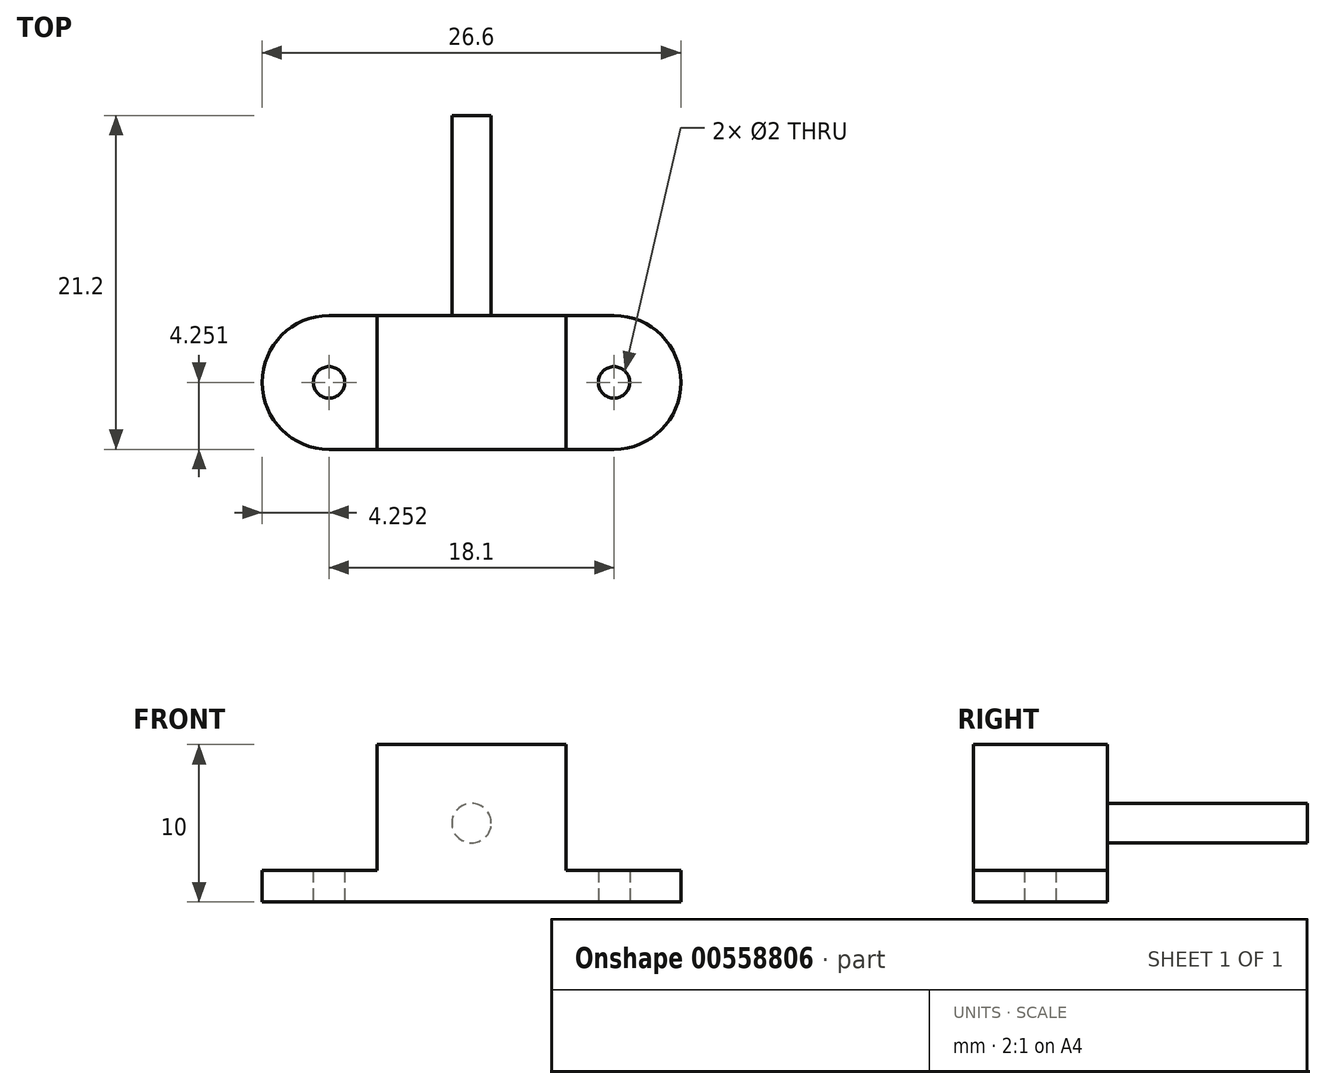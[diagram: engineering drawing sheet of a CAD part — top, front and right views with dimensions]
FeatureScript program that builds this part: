
annotation { "Feature Type Name" : "Feature", "Feature Type Description" : "" }
export const myFeature = defineFeature(function(context is Context, id is Id, definition is map)
    precondition{}
    {
        {
            var Q0;
            Q0=qCreatedBy(makeId("Top.planeOp"),FACE);
            var sketch = newSketch(context, id + "F0", { "sketchPlane" : qUnion([Q0])});
            skLineSegment(sketch, "E0.bottom", {"start": v(-10.3, -6.4) * mm, "end": v(16.3, -6.4) * mm});
            skLineSegment(sketch, "E0.top", {"start": v(-10.3, 2.1) * mm, "end": v(16.3, 2.1) * mm});
            skLineSegment(sketch, "E0.left", {"start": v(-10.3, -6.4) * mm, "end": v(-10.3, 2.1) * mm});
            skLineSegment(sketch, "E0.right", {"start": v(16.3, -6.4) * mm, "end": v(16.3, 2.1) * mm});
            skArc(sketch, "E1", {"start": v(-6.06, 2.1) * mm, "mid": v(-10.3, -2.15) * mm, "end": v(-6.06, -6.4) * mm});
            skArc(sketch, "E2", {"start": v(12.04, -6.4) * mm, "mid": v(16.3, -2.15) * mm, "end": v(12.04, 2.1) * mm});
            skCircle(sketch, "E3", {"center": v(-6.06, -2.15) * mm, "radius": 1 * mm});
            skCircle(sketch, "E4", {"center": v(12.04, -2.15) * mm, "radius": 1 * mm});
            skSolve(sketch);
        }
        {
            var Q0;
            Q0=makeQuery(id+"F0.imprint","IMPRINT",FACE,{"disambiguationData":[TD([[makeQuery(id+"F0.imprint","IMPRINT",EDGE,{"derivedFrom":sQuery(id+"F0.wireOp",EDGE,"E3")}),-1.0]])]});
            extrude(context, id + "F1", {"entities" : qUnion([Q0]), "depth" : 2 * mm, "offsetDistance" : 25.4 * mm});
        }
        {
            var Q0;
            Q0=makeQuery(id+"F1.opExtrude","CAP_FACE",FACE,{"disambiguationData":[OSD([sQuery(id+"F0.wireOp",EDGE,"E0.bottom"),sQuery(id+"F0.wireOp",EDGE,"E0.top"),sQuery(id+"F0.wireOp",EDGE,"E1"),sQuery(id+"F0.wireOp",EDGE,"E2"),sQuery(id+"F0.wireOp",EDGE,"E3"),sQuery(id+"F0.wireOp",EDGE,"E4")])],"isStart":false});
            var sketch = newSketch(context, id + "F2", { "sketchPlane" : qUnion([Q0])});
            skLineSegment(sketch, "E5.bottom", {"start": v(-10.3, -6.4) * mm, "end": v(16.3, -6.4) * mm});
            skLineSegment(sketch, "E5.top", {"start": v(-10.3, 2.1) * mm, "end": v(16.3, 2.1) * mm});
            skLineSegment(sketch, "E5.left", {"start": v(-10.3, -6.4) * mm, "end": v(-10.3, 2.1) * mm});
            skLineSegment(sketch, "E5.right", {"start": v(16.3, -6.4) * mm, "end": v(16.3, 2.1) * mm});
            skArc(sketch, "E6", {"start": v(-6.06, 2.1) * mm, "mid": v(-10.3, -2.15) * mm, "end": v(-6.06, -6.4) * mm});
            skArc(sketch, "E7", {"start": v(12.04, -6.4) * mm, "mid": v(16.3, -2.15) * mm, "end": v(12.04, 2.1) * mm});
            skCircle(sketch, "E8", {"center": v(-6.06, -2.15) * mm, "radius": 1 * mm});
            skCircle(sketch, "E9", {"center": v(12.04, -2.15) * mm, "radius": 1 * mm});
            skLineSegment(sketch, "E10", {"start": v(-3, -6.4) * mm, "end": v(-3, 2.1) * mm});
            skLineSegment(sketch, "E11", {"start": v(-3, 2.1) * mm, "end": v(9, 2.1) * mm});
            skLineSegment(sketch, "E12", {"start": v(9, 2.1) * mm, "end": v(9, -6.4) * mm});
            skLineSegment(sketch, "E13", {"start": v(9, -6.4) * mm, "end": v(-3, -6.4) * mm});
            skPoint(sketch, "E14.orphan", {"position": v(-3, 0.92) * mm});
            skPoint(sketch, "E15.orphan", {"position": v(9, 0.92) * mm});
            skSolve(sketch);
        }
        {
            var Q0;
            Q0=makeQuery(id+"F2.imprint","IMPRINT",FACE,{"disambiguationData":[TD([[makeQuery(id+"F2.imprint","IMPRINT",EDGE,{"derivedFrom":sQuery(id+"F2.wireOp",EDGE,"E10")}),-1.0]])]});
            extrude(context, id + "F3", {"entities" : qUnion([Q0]), "operationType" : NewBodyOperationType.ADD, "depth" : 8 * mm, "offsetDistance" : 25.4 * mm});
        }
        {
            var Q0;
            Q0=makeQuery(id+"F3.boolean.opBoolean","MERGE",FACE,{"derivedFrom":[makeQuery(id+"F1.opExtrude","SWEPT_FACE",FACE,{"disambiguationData":[OSD([sQuery(id+"F0.wireOp",EDGE,"E0.top")])]}),makeQuery(id+"F3.opExtrude","SWEPT_FACE",FACE,{"disambiguationData":[OSD([sQuery(id+"F2.wireOp",EDGE,"E11")])]})]});
            var sketch = newSketch(context, id + "F4", { "sketchPlane" : qUnion([Q0])});
            skCircle(sketch, "E16", {"center": v(-3, 5) * mm, "radius": 1.25 * mm});
            skSolve(sketch);
        }
        {
            var Q0;
            Q0=makeQuery(id+"F4.imprint","IMPRINT",FACE,{"disambiguationData":[TD([[makeQuery(id+"F4.imprint","IMPRINT",EDGE,{"derivedFrom":sQuery(id+"F4.wireOp",EDGE,"E16")}),1.0]])]});
            extrude(context, id + "F5", {"entities" : qUnion([Q0]), "operationType" : NewBodyOperationType.ADD, "depth" : 12.7 * mm, "offsetDistance" : 25.4 * mm});
        }
    });
